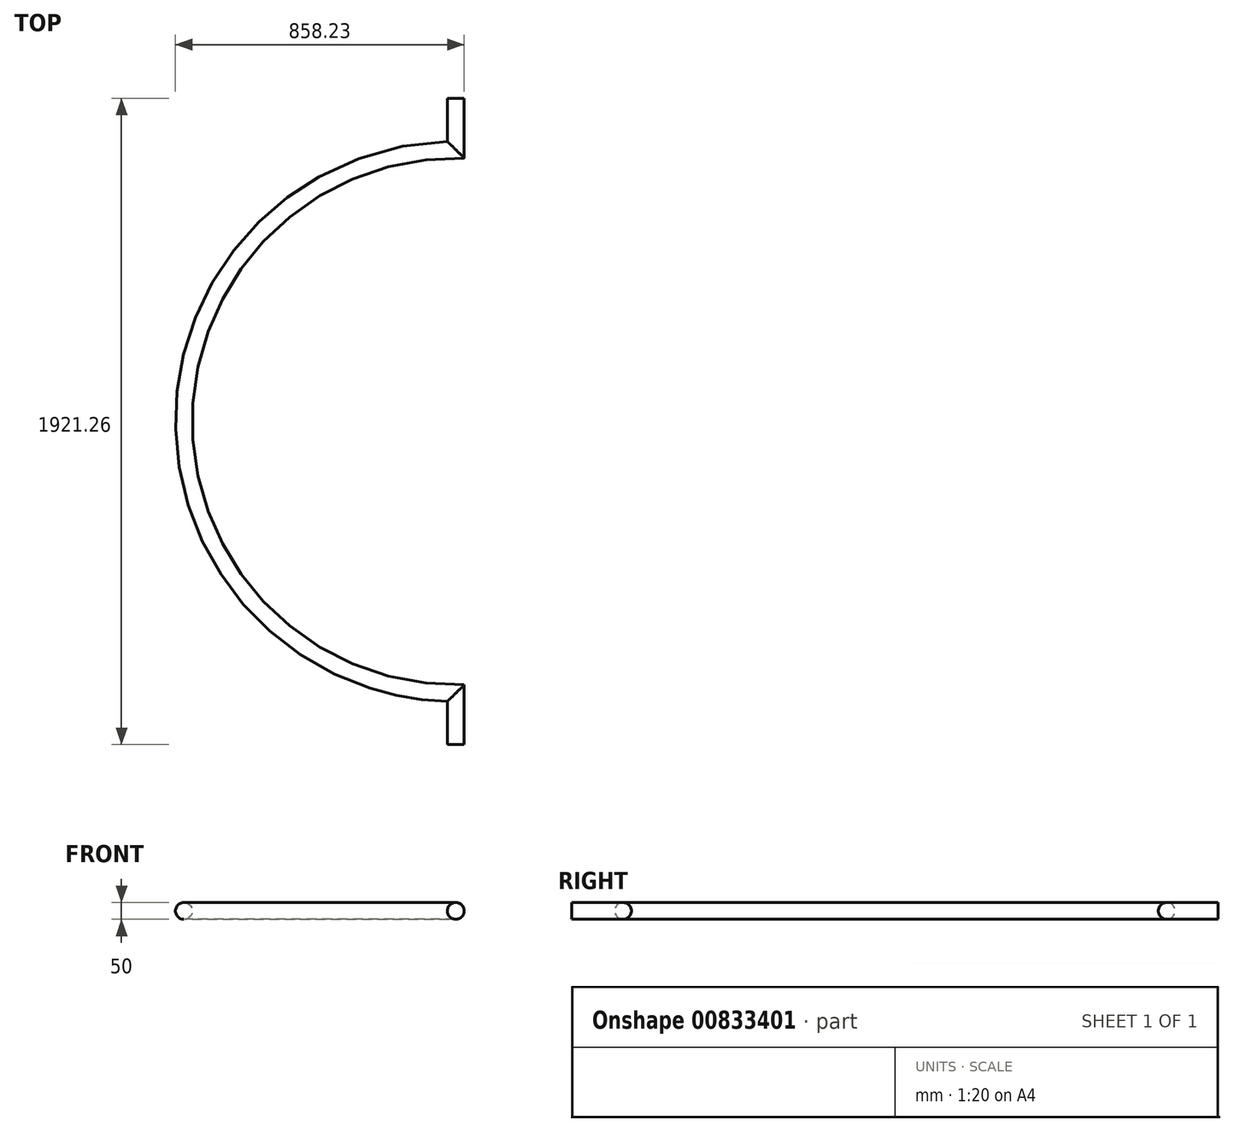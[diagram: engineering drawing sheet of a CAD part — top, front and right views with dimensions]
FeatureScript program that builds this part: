
annotation { "Feature Type Name" : "Feature", "Feature Type Description" : "" }
export const myFeature = defineFeature(function(context is Context, id is Id, definition is map)
    precondition{}
    {
        {
            var Q0;
            Q0=qCreatedBy(makeId("Top.planeOp"),FACE);
            var sketch = newSketch(context, id + "F0", { "sketchPlane" : qUnion([Q0])});
            skLineSegment(sketch, "E0", {"start": v(0, 0) * mm, "end": v(0, 152.4) * mm});
            skArc(sketch, "E1", {"start": v(0, 1768.86) * mm, "mid": v(-808.23, 960.63) * mm, "end": v(0, 152.4) * mm});
            skLineSegment(sketch, "E2", {"start": v(0, 1768.86) * mm, "end": v(0, 1921.26) * mm});
            skSolve(sketch);
        }
        {
            var Q0;
            Q0=qCreatedBy(makeId("Front.planeOp"),FACE);
            var sketch = newSketch(context, id + "F1", { "sketchPlane" : qUnion([Q0])});
            skCircle(sketch, "E3", {"center": v(0, 0) * mm, "radius": 25 * mm});
            skSolve(sketch);
        }
        {
            var Q0;
            Q0=makeQuery(id+"F1.imprint","IMPRINT",FACE,{"disambiguationData":[TD([[makeQuery(id+"F1.imprint","IMPRINT",EDGE,{"derivedFrom":sQuery(id+"F1.wireOp",EDGE,"E3")}),1.0]])]});
            var Q1;
            Q1=sQuery(id+"F0.wireOp",EDGE,"E0");
            var Q2;
            Q2=sQuery(id+"F0.wireOp",EDGE,"E1");
            var Q3;
            Q3=sQuery(id+"F0.wireOp",EDGE,"E2");
            sweep(context, id + "F2", {"profiles" : qUnion([Q0]), "path" : qUnion([Q1, Q2, Q3])});
        }
    });
